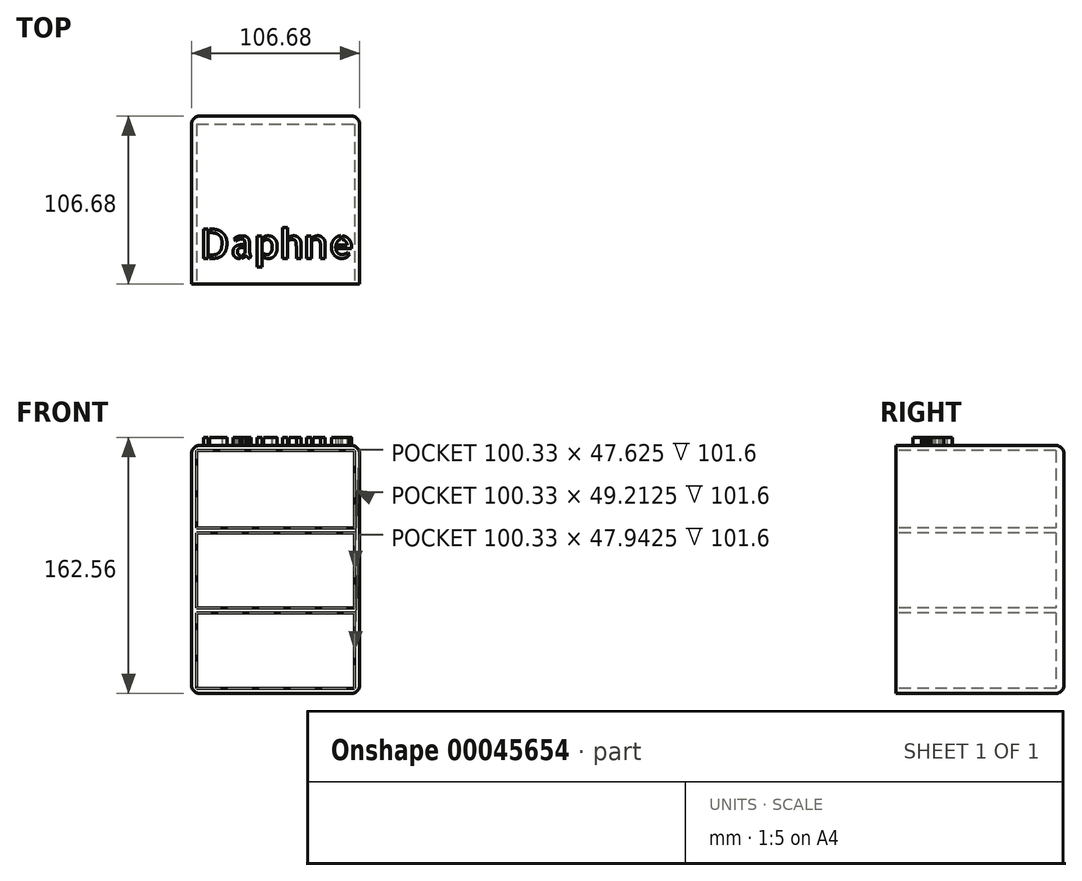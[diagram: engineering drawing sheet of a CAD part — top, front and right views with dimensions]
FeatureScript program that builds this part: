
annotation { "Feature Type Name" : "Feature", "Feature Type Description" : "" }
export const myFeature = defineFeature(function(context is Context, id is Id, definition is map)
    precondition{}
    {
        {
            var Q0;
            Q0=qCreatedBy(makeId("Front.planeOp"),FACE);
            var sketch = newSketch(context, id + "F0", { "sketchPlane" : qUnion([Q0])});
            skLineSegment(sketch, "E0.bottom", {"start": v(-51.12, 110.97) * mm, "end": v(55.56, 110.97) * mm});
            skLineSegment(sketch, "E0.top", {"start": v(-51.12, -46.51) * mm, "end": v(55.56, -46.51) * mm});
            skLineSegment(sketch, "E0.left", {"start": v(-51.12, 110.97) * mm, "end": v(-51.12, -46.51) * mm});
            skLineSegment(sketch, "E0.right", {"start": v(55.56, 110.97) * mm, "end": v(55.56, -46.51) * mm});
            skSolve(sketch);
        }
        {
            var Q0;
            Q0=qSketchRegion(id+"F0",true);
            extrude(context, id + "F1", {"entities" : qUnion([Q0]), "depth" : 106.68 * mm});
        }
        {
            var Q0;
            Q0=makeQuery(id+"F1.opExtrude","CAP_FACE",FACE,{"disambiguationData":[OSD([sQuery(id+"F0.wireOp",EDGE,"E0.bottom"),sQuery(id+"F0.wireOp",EDGE,"E0.top"),sQuery(id+"F0.wireOp",EDGE,"E0.left"),sQuery(id+"F0.wireOp",EDGE,"E0.right")])],"isStart":false});
            var sketch = newSketch(context, id + "F2", { "sketchPlane" : qUnion([Q0])});
            skLineSegment(sketch, "E1.bottom", {"start": v(-47.94, 107.8) * mm, "end": v(52.39, 107.8) * mm});
            skLineSegment(sketch, "E1.top", {"start": v(-47.94, -43.34) * mm, "end": v(52.39, -43.34) * mm});
            skLineSegment(sketch, "E1.left", {"start": v(-47.94, 107.8) * mm, "end": v(-47.94, -43.34) * mm});
            skLineSegment(sketch, "E1.right", {"start": v(52.39, 107.8) * mm, "end": v(52.39, -43.34) * mm});
            skSolve(sketch);
        }
        {
            var Q0;
            Q0=qSketchRegion(id+"F2",true);
            extrude(context, id + "F3", {"entities" : qUnion([Q0]), "operationType" : NewBodyOperationType.REMOVE, "oppositeDirection" : true, "depth" : 101.6 * mm});
        }
        {
            var Q0;
            Q0=makeQuery(id+"F1.opExtrude","CAP_FACE",FACE,{"disambiguationData":[OSD([sQuery(id+"F0.wireOp",EDGE,"E0.bottom"),sQuery(id+"F0.wireOp",EDGE,"E0.top"),sQuery(id+"F0.wireOp",EDGE,"E0.left"),sQuery(id+"F0.wireOp",EDGE,"E0.right")])],"isStart":false});
            var sketch = newSketch(context, id + "F4", { "sketchPlane" : qUnion([Q0])});
            skLineSegment(sketch, "E2.bottom", {"start": v(-51.12, 55.4) * mm, "end": v(55.56, 55.4) * mm});
            skLineSegment(sketch, "E2.top", {"start": v(-51.12, 58.58) * mm, "end": v(55.56, 58.58) * mm});
            skLineSegment(sketch, "E2.left", {"start": v(-51.12, 58.58) * mm, "end": v(-51.12, 55.4) * mm});
            skLineSegment(sketch, "E2.right", {"start": v(55.56, 58.58) * mm, "end": v(55.56, 55.4) * mm});
            skLineSegment(sketch, "E3.bottom", {"start": v(-51.12, 7.78) * mm, "end": v(55.56, 7.78) * mm});
            skLineSegment(sketch, "E3.top", {"start": v(-51.12, 4.6) * mm, "end": v(55.56, 4.6) * mm});
            skLineSegment(sketch, "E3.left", {"start": v(-51.12, 7.78) * mm, "end": v(-51.12, 4.6) * mm});
            skLineSegment(sketch, "E3.right", {"start": v(55.56, 7.78) * mm, "end": v(55.56, 4.6) * mm});
            skLineSegment(sketch, "E4", {"start": v(55.56, 6.2) * mm, "end": v(-51.12, 6.2) * mm});
            skLineSegment(sketch, "E5", {"start": v(-51.12, 57) * mm, "end": v(55.56, 57) * mm});
            skSolve(sketch);
        }
        {
            var Q0;
            Q0=qSketchRegion(id+"F4",true);
            extrude(context, id + "F5", {"entities" : qUnion([Q0]), "operationType" : NewBodyOperationType.ADD, "oppositeDirection" : true, "depth" : 101.6 * mm});
        }
        {
            var Q0;
            Q0=makeQuery(id+"F1.opExtrude","SWEPT_EDGE",EDGE,{"disambiguationData":[OSD([sQuery(id+"F0.wireOp",EDGE,"E0.bottom"),sQuery(id+"F0.wireOp",EDGE,"E0.right")])]});
            var Q1;
            Q1=makeQuery(id+"F1.opExtrude","SWEPT_EDGE",EDGE,{"disambiguationData":[OSD([sQuery(id+"F0.wireOp",EDGE,"E0.bottom"),sQuery(id+"F0.wireOp",EDGE,"E0.left")])]});
            var Q2;
            Q2=makeQuery(id+"F1.opExtrude","SWEPT_EDGE",EDGE,{"disambiguationData":[OSD([sQuery(id+"F0.wireOp",EDGE,"E0.top"),sQuery(id+"F0.wireOp",EDGE,"E0.right")])]});
            var Q3;
            Q3=makeQuery(id+"F1.opExtrude","SWEPT_EDGE",EDGE,{"disambiguationData":[OSD([sQuery(id+"F0.wireOp",EDGE,"E0.top"),sQuery(id+"F0.wireOp",EDGE,"E0.left")])]});
            var Q4;
            Q4=makeQuery(id+"F1.opExtrude","CAP_EDGE",EDGE,{"disambiguationData":[OSD([sQuery(id+"F0.wireOp",EDGE,"E0.left")])],"isStart":true});
            var Q5;
            Q5=makeQuery(id+"F1.opExtrude","CAP_EDGE",EDGE,{"disambiguationData":[OSD([sQuery(id+"F0.wireOp",EDGE,"E0.bottom")])],"isStart":true});
            var Q6;
            Q6=makeQuery(id+"F1.opExtrude","CAP_EDGE",EDGE,{"disambiguationData":[OSD([sQuery(id+"F0.wireOp",EDGE,"E0.right")])],"isStart":true});
            var Q7;
            Q7=makeQuery(id+"F1.opExtrude","CAP_EDGE",EDGE,{"disambiguationData":[OSD([sQuery(id+"F0.wireOp",EDGE,"E0.top")])],"isStart":true});
            fillet(context, id + "F6", {"entities" : qUnion([Q0, Q1, Q2, Q3, Q4, Q5, Q6, Q7]), "radius" : 5.08 * mm, "tangentPropagation" : true, "allowEdgeOverflow" : false});
        }
        {
            var Q0;
            Q0=makeQuery(id+"F1.opExtrude","SWEPT_FACE",FACE,{"disambiguationData":[OSD([sQuery(id+"F0.wireOp",EDGE,"E0.bottom")])]});
            var sketch = newSketch(context, id + "F7", { "sketchPlane" : qUnion([Q0])});
            skText(sketch, "E6", { "text": "Daphne", "fontName": "AllertaStencil-Regular.ttf"});
            const initialGuessF7  = {"E6": [-0.04604, -0.09035, 1, 0, 0.01855]};
            skSetInitialGuess(sketch, initialGuessF7);
            skSolve(sketch);
        }
        {
            var Q0;
            Q0 = qSketchRegion(id + "F7", true);
            extrude(context, id + "F8", {"entities" : qUnion([Q0]), "operationType" : NewBodyOperationType.ADD, "depth" : 5.08 * mm});
        }
    });
